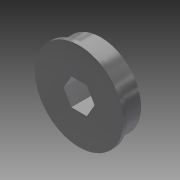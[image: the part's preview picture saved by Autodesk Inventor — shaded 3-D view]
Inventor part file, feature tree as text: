
AUTODESK INVENTOR PART (.ipt)
format: ipt  version: 2014 (Build 180170000, 170)  size: 116,736 bytes
history: native  units: in
note: dims shown in document units (in); Inventor stores cm internally (conversion verified against a paired STEP export)
features: extrude x2, sketch x2
ambient origin geometry x8: Origin, YZ Plane, XZ Plane, XY Plane, X Axis, Y Axis, Z Axis, Center Point
bodies: Solid1 (feature_tree)
feature tree (4):
  extrude  "Extrusion1"  Depth=0.375in
  extrude  "Extrusion2"  Depth=0.055in
  sketch  "Sketch1"  dims[d0=0.375in d1=1.125in]
  sketch  "Sketch2"  dims[d2=0.25in d3=0.0in d4=0.055in d5=0.055in d6=0.0in]
